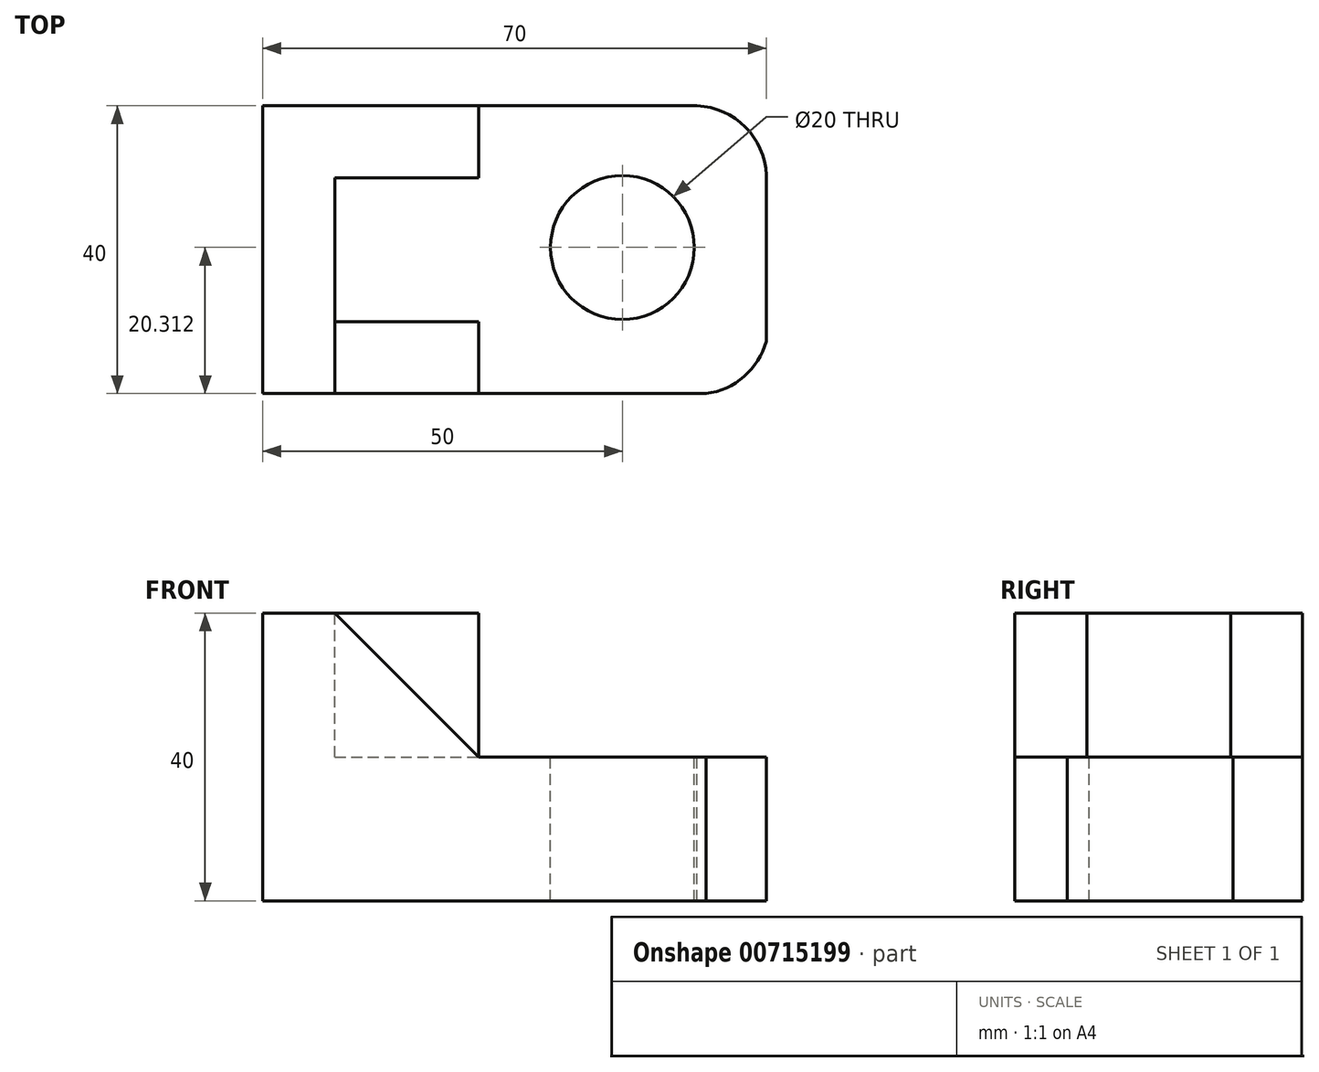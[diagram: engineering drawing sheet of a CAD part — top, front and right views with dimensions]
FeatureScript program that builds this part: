
annotation { "Feature Type Name" : "Feature", "Feature Type Description" : "" }
export const myFeature = defineFeature(function(context is Context, id is Id, definition is map)
    precondition{}
    {
        {
            var Q0;
            Q0=qCreatedBy(makeId("Front.planeOp"),FACE);
            var sketch = newSketch(context, id + "F0", { "sketchPlane" : qUnion([Q0])});
            skLineSegment(sketch, "E0", {"start": v(0, 0) * mm, "end": v(70, 0) * mm});
            skLineSegment(sketch, "E1", {"start": v(70, 0) * mm, "end": v(70, 20) * mm});
            skLineSegment(sketch, "E2", {"start": v(70, 20) * mm, "end": v(30, 20) * mm});
            skLineSegment(sketch, "E3", {"start": v(30, 20) * mm, "end": v(30, 40) * mm});
            skLineSegment(sketch, "E4", {"start": v(30, 40) * mm, "end": v(0, 40) * mm});
            skLineSegment(sketch, "E5", {"start": v(0, 40) * mm, "end": v(0, 0) * mm});
            skSolve(sketch);
        }
        {
            var Q0;
            Q0=makeQuery(id+"F0.imprint","IMPRINT",FACE,{"disambiguationData":[TD([[makeQuery(id+"F0.imprint","IMPRINT",EDGE,{"derivedFrom":sQuery(id+"F0.wireOp",EDGE,"E0")}),1.0]])]});
            extrude(context, id + "F1", {"entities" : qUnion([Q0]), "depth" : 40 * mm, "offsetDistance" : 25 * mm});
        }
        {
            var Q0;
            Q0=makeQuery(id+"F1.opExtrude","CAP_FACE",FACE,{"disambiguationData":[OSD([sQuery(id+"F0.wireOp",EDGE,"E0"),sQuery(id+"F0.wireOp",EDGE,"E1"),sQuery(id+"F0.wireOp",EDGE,"E2"),sQuery(id+"F0.wireOp",EDGE,"E3"),sQuery(id+"F0.wireOp",EDGE,"E4"),sQuery(id+"F0.wireOp",EDGE,"E5")])],"isStart":false});
            var sketch = newSketch(context, id + "F2", { "sketchPlane" : qUnion([Q0])});
            skLineSegment(sketch, "E6", {"start": v(30, 40) * mm, "end": v(10, 40) * mm});
            skLineSegment(sketch, "E7", {"start": v(10, 40) * mm, "end": v(30, 20) * mm});
            skLineSegment(sketch, "E8", {"start": v(30, 20) * mm, "end": v(30, 40) * mm});
            skSolve(sketch);
        }
        {
            var Q0;
            Q0=makeQuery(id+"F2.imprint","IMPRINT",FACE,{"disambiguationData":[TD([[makeQuery(id+"F2.imprint","IMPRINT",EDGE,{"derivedFrom":sQuery(id+"F2.wireOp",EDGE,"E6")}),1.0]])]});
            extrude(context, id + "F3", {"entities" : qUnion([Q0]), "operationType" : NewBodyOperationType.REMOVE, "oppositeDirection" : true, "depth" : 10 * mm, "offsetDistance" : 25 * mm});
        }
        {
            var Q0;
            Q0=makeQuery(id+"F1.opExtrude","SWEPT_FACE",FACE,{"disambiguationData":[OSD([sQuery(id+"F0.wireOp",EDGE,"E4")])]});
            var sketch = newSketch(context, id + "F4", { "sketchPlane" : qUnion([Q0])});
            skLineSegment(sketch, "E9", {"start": v(10, -30) * mm, "end": v(10, -10) * mm});
            skLineSegment(sketch, "E10", {"start": v(10, -10) * mm, "end": v(30, -10) * mm});
            skLineSegment(sketch, "E11", {"start": v(30, -10) * mm, "end": v(30, -30) * mm});
            skLineSegment(sketch, "E12", {"start": v(30, -30) * mm, "end": v(10, -30) * mm});
            skSolve(sketch);
        }
        {
            var Q0;
            Q0=makeQuery(id+"F4.imprint","IMPRINT",FACE,{"disambiguationData":[TD([[makeQuery(id+"F4.imprint","IMPRINT",EDGE,{"derivedFrom":sQuery(id+"F4.wireOp",EDGE,"E9")}),-1.0]])]});
            extrude(context, id + "F5", {"entities" : qUnion([Q0]), "operationType" : NewBodyOperationType.REMOVE, "oppositeDirection" : true, "depth" : 20 * mm, "offsetDistance" : 25 * mm});
        }
        {
            var Q0;
            Q0=makeQuery(id+"F5.boolean.opBoolean","MERGE",FACE,{"derivedFrom":[makeQuery(id+"F1.opExtrude","SWEPT_FACE",FACE,{"disambiguationData":[OSD([sQuery(id+"F0.wireOp",EDGE,"E2")])]}),makeQuery(id+"F5.opExtrude","CAP_FACE",FACE,{"disambiguationData":[OSD([sQuery(id+"F4.wireOp",EDGE,"E9"),sQuery(id+"F4.wireOp",EDGE,"E10"),sQuery(id+"F4.wireOp",EDGE,"E11"),sQuery(id+"F4.wireOp",EDGE,"E12")])],"isStart":false})]});
            var sketch = newSketch(context, id + "F6", { "sketchPlane" : qUnion([Q0])});
            skArc(sketch, "E13", {"start": v(70, -10.34) * mm, "mid": v(67.07, -2.91) * mm, "end": v(59.63, 0) * mm});
            skSolve(sketch);
        }
        {
            var Q0;
            {var subQ0=sQuery(id+"F6.wireOp",EDGE,"E13");var subQ1=sQuery(id+"F0.wireOp",EDGE,"E2");var subQ4=makeQuery(id+"F1.opExtrude","CAP_EDGE",EDGE,{"disambiguationData":[OSD([subQ1])],"isStart":true});var subQ5=makeQuery(id+"F6.imprint","INTERSECT",VERTEX,{"disambiguationData":[OD(1.0)],"derivedFrom":[subQ4,subQ0]});Q0=makeQuery(id+"F6.imprint","IMPRINT",FACE,{"disambiguationData":[TD([[makeQuery(id+"F6.imprint","IMPRINT",EDGE,{"disambiguationData":[TD([[subQ5,1.0]])],"derivedFrom":subQ0}),-1.0]])]});}
            extrude(context, id + "F7", {"entities" : qUnion([Q0]), "operationType" : NewBodyOperationType.REMOVE, "oppositeDirection" : true, "depth" : 20 * mm, "offsetDistance" : 25 * mm});
        }
        {
            var Q0;
            Q0=makeQuery(id+"F5.boolean.opBoolean","MERGE",FACE,{"derivedFrom":[makeQuery(id+"F1.opExtrude","SWEPT_FACE",FACE,{"disambiguationData":[OSD([sQuery(id+"F0.wireOp",EDGE,"E2")])]}),makeQuery(id+"F5.opExtrude","CAP_FACE",FACE,{"disambiguationData":[OSD([sQuery(id+"F4.wireOp",EDGE,"E9"),sQuery(id+"F4.wireOp",EDGE,"E10"),sQuery(id+"F4.wireOp",EDGE,"E11"),sQuery(id+"F4.wireOp",EDGE,"E12")])],"isStart":false})]});
            var sketch = newSketch(context, id + "F8", { "sketchPlane" : qUnion([Q0])});
            skArc(sketch, "E14", {"start": v(61.61, -40) * mm, "mid": v(66.91, -37.63) * mm, "end": v(70, -32.72) * mm});
            skSolve(sketch);
        }
        {
            var Q0;
            {var subQ0=sQuery(id+"F8.wireOp",EDGE,"E14");Q0=makeQuery(id+"F8.imprint","IMPRINT",FACE,{"disambiguationData":[TD([[makeQuery(id+"F8.imprint","IMPRINT",EDGE,{"derivedFrom":subQ0}),-1.0]])]});}
            extrude(context, id + "F9", {"entities" : qUnion([Q0]), "operationType" : NewBodyOperationType.REMOVE, "oppositeDirection" : true, "depth" : 20 * mm, "offsetDistance" : 25 * mm});
        }
        {
            var Q0;
            Q0=makeQuery(id+"F5.boolean.opBoolean","MERGE",FACE,{"derivedFrom":[makeQuery(id+"F1.opExtrude","SWEPT_FACE",FACE,{"disambiguationData":[OSD([sQuery(id+"F0.wireOp",EDGE,"E2")])]}),makeQuery(id+"F5.opExtrude","CAP_FACE",FACE,{"disambiguationData":[OSD([sQuery(id+"F4.wireOp",EDGE,"E9"),sQuery(id+"F4.wireOp",EDGE,"E10"),sQuery(id+"F4.wireOp",EDGE,"E11"),sQuery(id+"F4.wireOp",EDGE,"E12")])],"isStart":false})]});
            var sketch = newSketch(context, id + "F10", { "sketchPlane" : qUnion([Q0])});
            skCircle(sketch, "E15", {"center": v(50, -19.69) * mm, "radius": 10 * mm});
            skLineSegment(sketch, "E16", {"start": v(50, -19.69) * mm, "end": v(50, -40) * mm});
            skLineSegment(sketch, "E17", {"start": v(50, -40) * mm, "end": v(0, -40) * mm});
            skSolve(sketch);
        }
        {
            var Q0;
            Q0=makeQuery(id+"F10.imprint","IMPRINT",FACE,{"disambiguationData":[TD([[makeQuery(id+"F10.imprint","IMPRINT",EDGE,{"derivedFrom":sQuery(id+"F10.wireOp",EDGE,"E15")}),1.0]])]});
            extrude(context, id + "F11", {"entities" : qUnion([Q0]), "operationType" : NewBodyOperationType.REMOVE, "oppositeDirection" : true, "depth" : 20 * mm, "offsetDistance" : 25 * mm});
        }
    });
